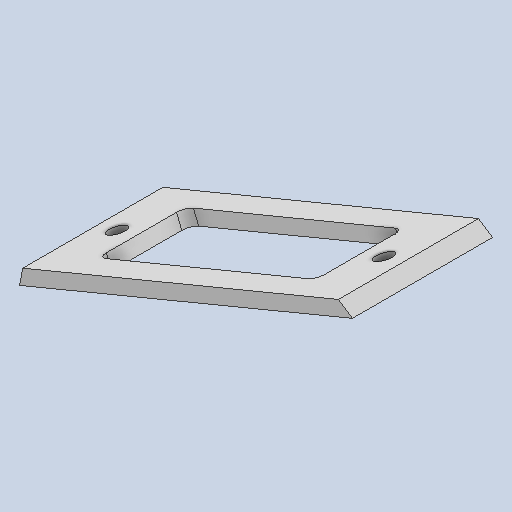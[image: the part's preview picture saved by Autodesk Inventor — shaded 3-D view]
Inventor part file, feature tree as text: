
AUTODESK INVENTOR PART (.ipt)
format: ipt  version: 2025 (Build 290162010, 162A)  size: 124,416 bytes
history: native  units: mm
features: extrude x2, sketch x2, fillet x1
ambient origin geometry x8: Origin, YZ Plane, XZ Plane, XY Plane, X Axis, Y Axis, Z Axis, Center Point
bodies: Solid1 (feature_tree)
feature tree (5):
  extrude  "Extrusion1"  Depth=5.0mm
  extrude  "Extrusion2"  Depth=80.0mm
  fillet  "Fillet1"  [1 undecoded]
  sketch  "Sketch2"  dims[d0=513.0mm d1=260.0mm d2=635.0mm d6=5.0mm]
  sketch  "Sketch3"  dims[d7=8.0mm d8=80.0mm d9=0.0mm d10=135.0mm d11=10.0mm d12=15.0mm d13=50.0mm d14=0.0mm d15=0.0mm d16=5.0mm]
note: 1 required parameter value undecoded (feature->parameter linkage not recoverable at this tier; creation-order binding heuristic only, values carry confidence <= 0.55)
